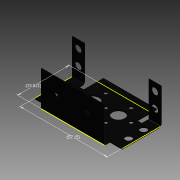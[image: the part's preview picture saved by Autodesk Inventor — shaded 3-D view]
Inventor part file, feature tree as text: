
AUTODESK INVENTOR PART (.ipt)
format: ipt  version: 2015 (Build 190159000, 159)  size: 262,144 bytes
history: native  units: in
note: dims shown in document units (in); Inventor stores cm internally (conversion verified against a paired STEP export)
features: other x7, direct_edit x4, fillet x1, sketch x1, imported_body x1, move_body x1
ambient origin geometry x8: Origin, YZ Plane, XZ Plane, XY Plane, X Axis, Y Axis, Z Axis, Center Point
bodies: Body1 (feature_tree)
feature tree (15):
  fillet  "Fillet5"  [1 undecoded]
  other  "asb-041"
  direct_edit  "Direct Edit1"
  direct_edit  "Direct Edit2"
  direct_edit  "Direct Edit3"
  sketch  "Sketch7"  dims[d8=-0.0394in d9=-0.0354in d10=0.0039in d11=0.0039in d12=-0.0394in d16=1.3316in d17=2.25in d18=0.0in d19=0.0in d20=0.1575in]
  direct_edit  "Direct Edit4"
  imported_body  "Base1"
  other  "Size1"
  other  "Size2"
  other  "Size3"
  other  "Size4"
  other  "Size5"
  other  "Size6"
  move_body  "Move1"
note: 1 required parameter value undecoded (feature->parameter linkage not recoverable at this tier; creation-order binding heuristic only, values carry confidence <= 0.55)
